FCSTD DOCUMENT  (FreeCAD 1.0R38806 (Git))
Label: UTDFN-4
License: All rights reserved
LicenseURL: http://en.wikipedia.org/wiki/All_rights_reserved
objects: Sketcher::SketchObject×1, PartDesign::Body×1
note: 3 computed .brp shape members not serialized (recipe doc carries the construction recipe); baked Part::Feature solids carry a one-line shape summary decoded from their .brp

FEATURE [Sketcher::SketchObject] Sketch
  ArcFitTolerance = 1e-06
  AttachmentSupport = -> [XY_Plane]
  FullyConstrained = false
  MakeInternals = false
  MapMode = 5
  sketch-geometry (40):
    g0: LineSegment StartX=0 StartY=0.339411 StartZ=0 EndX=-0.339411 EndY=0 EndZ=0
    g1: LineSegment StartX=-0.339411 StartY=0 StartZ=0 EndX=0 EndY=-0.339411 EndZ=0
    g2: LineSegment StartX=0 StartY=-0.339411 StartZ=0 EndX=0.0707107 EndY=-0.268701 EndZ=0
    g3: LineSegment StartX=0.339411 StartY=0 StartZ=0 EndX=0 EndY=0.339411 EndZ=0
    g4: Circle [constr] CenterX=0 CenterY=0 CenterZ=0 NormalX=0 NormalY=0 NormalZ=1 AngleXU=0 Radius=0.339411
    g5: LineSegment [constr] StartX=-0.689647 StartY=-0.350236 StartZ=0 EndX=0.278575 EndY=0.617986 EndZ=0
    g6: LineSegment [constr] StartX=-0.310589 StartY=-0.65 StartZ=0 EndX=0.770537 EndY=0.431126 EndZ=0
    g7: LineSegment [constr] StartX=0.56807 StartY=-0.228658 StartZ=0 EndX=-0.256476 EndY=0.595887 EndZ=0
    g8: LineSegment [constr] StartX=-0.605191 StartY=0.26578 StartZ=0 EndX=0.310589 EndY=-0.65 EndZ=0
    g9: LineSegment [constr] StartX=-0.027746 StartY=-0.65 StartZ=0 EndX=0.673358 EndY=0.0511041 EndZ=0
    g10: LineSegment [constr] StartX=-0.650384 StartY=-0.0281301 StartZ=0 EndX=0.027746 EndY=0.65 EndZ=0
    g11: LineSegment [constr] StartX=-0.027746 StartY=0.65 StartZ=0 EndX=0.785591 EndY=-0.163337 EndZ=0
    g12: LineSegment [constr] StartX=-0.772254 StartY=0.15 StartZ=0 EndX=0.027746 EndY=-0.65 EndZ=0
    g13: LineSegment [constr] StartX=-0.325 StartY=0.65 StartZ=0 EndX=-0.325 EndY=-0.65 EndZ=0
    g14: LineSegment [constr] StartX=-0.325 StartY=-0.65 StartZ=0 EndX=0.325 EndY=-0.65 EndZ=0
    g15: LineSegment [constr] StartX=0.325 StartY=-0.65 StartZ=0 EndX=0.325 EndY=0.65 EndZ=0
    g16: LineSegment [constr] StartX=0.325 StartY=0.65 StartZ=0 EndX=-0.325 EndY=0.65 EndZ=0
    g17: LineSegment StartX=0.2 StartY=-0.65 StartZ=0 EndX=0.45 EndY=-0.65 EndZ=0
    g18: LineSegment StartX=0.45 StartY=-0.65 StartZ=0 EndX=0.45 EndY=-0.25 EndZ=0
    g19: LineSegment StartX=0.45 StartY=-0.25 StartZ=0 EndX=0.372254 EndY=-0.25 EndZ=0
    g20: LineSegment StartX=-0.2 StartY=-0.65 StartZ=0 EndX=-0.2 EndY=-0.422254 EndZ=0
    g21: LineSegment StartX=-0.45 StartY=-0.25 StartZ=0 EndX=-0.45 EndY=-0.65 EndZ=0
    g22: LineSegment StartX=-0.45 StartY=-0.65 StartZ=0 EndX=-0.2 EndY=-0.65 EndZ=0
    g23: LineSegment StartX=-0.2 StartY=0.65 StartZ=0 EndX=-0.45 EndY=0.65 EndZ=0
    g24: LineSegment StartX=-0.45 StartY=0.65 StartZ=0 EndX=-0.45 EndY=0.25 EndZ=0
    g25: LineSegment StartX=-0.45 StartY=0.25 StartZ=0 EndX=-0.372254 EndY=0.25 EndZ=0
    g26: LineSegment StartX=0.2 StartY=0.65 StartZ=0 EndX=0.2 EndY=0.422254 EndZ=0
    g27: LineSegment StartX=0.372254 StartY=0.25 StartZ=0 EndX=0.45 EndY=0.25 EndZ=0
    g28: LineSegment StartX=0.45 StartY=0.25 StartZ=0 EndX=0.45 EndY=0.65 EndZ=0
    g29: LineSegment StartX=0.45 StartY=0.65 StartZ=0 EndX=0.2 EndY=0.65 EndZ=0
    g30: LineSegment StartX=-0.372254 StartY=-0.25 StartZ=0 EndX=-0.2 EndY=-0.422254 EndZ=0
    g31: LineSegment StartX=0.2 StartY=-0.422254 StartZ=0 EndX=0.372254 EndY=-0.25 EndZ=0
    g32: LineSegment StartX=-0.372254 StartY=0.25 StartZ=0 EndX=-0.2 EndY=0.422254 EndZ=0
    g33: LineSegment StartX=0.2 StartY=0.422254 StartZ=0 EndX=0.372254 EndY=0.25 EndZ=0
    g34: LineSegment StartX=-0.2 StartY=0.539411 StartZ=0 EndX=-0.2 EndY=0.65 EndZ=0
    g35: LineSegment StartX=0.2 StartY=-0.422254 StartZ=0 EndX=0.2 EndY=-0.65 EndZ=0
    g36: LineSegment StartX=-0.372254 StartY=-0.25 StartZ=0 EndX=-0.45 EndY=-0.25 EndZ=0
    g37: LineSegment StartX=-0.2 StartY=0.539411 StartZ=0 EndX=-0.2 EndY=0.422254 EndZ=0
    g38: ArcOfCircle CenterX=0.106066 CenterY=-0.233345 CenterZ=0 NormalX=0 NormalY=0 NormalZ=1 AngleXU=0 Radius=0.05 StartAngle=0.785398 EndAngle=3.92699
    g39: LineSegment StartX=0.141421 StartY=-0.19799 StartZ=0 EndX=0.339411 EndY=0 EndZ=0
  constraints (120):
    c: Coincident(g0,g1)
    c: Coincident(g1,g2)
    c: Coincident(g39,g3)
    c: Coincident(g3,g0)
    c: Equal(g0,g1)
    c: Equal(g0,g3)
    c: PointOnObject(g0,g4)
    c: PointOnObject(g1,g4)
    c: PointOnObject(g39,g4)
    c: PointOnObject(g3,g4)
    c: Coincident(g4,g-1)
    c: PointOnObject(g3,g-2)
    c: Distance(g3,g3) = 0.48
    c: Parallel(g8,g7)
    c: Parallel(g6,g5)
    c: PointOnObject(g0,g5)
    c: PointOnObject(g39,g6)
    c: PointOnObject(g1,g6)
    c: Perpendicular(g5,g8)
    c: PointOnObject(g1,g8)
    c: PointOnObject(g0,g7)
    c: Parallel(g12,g8)
    c: Parallel(g7,g11)
    c: Parallel(g10,g5)
    c: Parallel(g9,g6)
    c: Distance(g6,g9) = 0.2
    c: Distance(g11,g7) = 0.2
    c: Distance(g5,g10) = 0.2
    c: Distance(g8,g12) = 0.2
    c: Coincident(g13,g14)
    c: Coincident(g14,g15)
    c: Coincident(g15,g16)
    c: Coincident(g16,g13)
    c: Vertical(g13)
    c: Horizontal(g16)
    c: DistanceY(g15,g15) = 1.3
    c: Symmetric(g14,g15,g-1)
    c: PointOnObject(g10,g16)
    c: PointOnObject(g11,g16)
    c: DistanceX(g14,g14) = 0.65
    c: Symmetric(g14,g13,g-2)
    c: PointOnObject(g9,g14)
    c: PointOnObject(g12,g14)
    c: PointOnObject(g8,g14)
    c: PointOnObject(g6,g14)
    c: Coincident(g17,g18)
    c: Coincident(g18,g19)
    c: Coincident(g35,g17)
    c: Vertical(g18)
    c: Distance(g18,g35) = 0.25
    c: PointOnObject(g17,g14)
    c: Coincident(g36,g21)
    c: Coincident(g21,g22)
    c: Coincident(g22,g20)
    c: Vertical(g20)
    c: Vertical(g21)
    c: Distance(g20,g21) = 0.25
    c: Coincident(g23,g24)
    c: Coincident(g24,g25)
    c: Coincident(g34,g23)
    c: Vertical(g24)
    c: Distance(g24,g34) = 0.25
    c: PointOnObject(g23,g16)
    c: Coincident(g27,g28)
    c: Coincident(g28,g29)
    c: Coincident(g29,g26)
    c: Vertical(g26)
    c: Vertical(g28)
    c: Distance(g26,g28) = 0.25
    c: PointOnObject(g26,g16)
    c: Equal(g21,g24)
    c: Equal(g24,g28)
    c: Equal(g28,g18)
    c: DistanceY(g18,g18) = 0.4
    c: PointOnObject(g20,g14)
    c: Symmetric(g12,g12,g30)
    c: PointOnObject(g30,g12)
    c: PointOnObject(g31,g9)
    c: PointOnObject(g31,g9)
    c: PointOnObject(g32,g10)
    c: PointOnObject(g32,g10)
    c: PointOnObject(g33,g11)
    c: PointOnObject(g33,g11)
    c: PointOnObject(g33,g27)
    c: PointOnObject(g32,g34)
    c: PointOnObject(g32,g25)
    c: PointOnObject(g30,g36)
    c: PointOnObject(g30,g20)
    c: PointOnObject(g31,g35)
    c: PointOnObject(g31,g19)
    c: PointOnObject(g25,g10)
    c: PointOnObject(g34,g7)
    c: Coincident(g26,g33)
    c: PointOnObject(g27,g11)
    c: PointOnObject(g35,g9)
    c: PointOnObject(g19,g9)
    c: PointOnObject(g20,g12)
    c: PointOnObject(g36,g12)
    c: Coincident(g37,g32)
    c: Vertical(g37)
    c: Coincident(g37,g34)
    c: Symmetric(g23,g23,g13)
    c: Horizontal(g25)
    c: Symmetric(g26,g28,g15)
    c: Horizontal(g27)
    c: Symmetric(g20,g21,g13)
    c: Horizontal(g36)
    c: Symmetric(g17,g17,g15)
    c: Vertical(g35)
    c: Horizontal(g19)
    c: PointOnObject(g38,g2)
    c: Diameter(g38) = 0.1
    c: PointOnObject(g38,g6)
    c: PointOnObject(g38,g39)
    c: PointOnObject(g2,g38)
    c: PointOnObject(g39,g38)
    c: Parallel(g1,g8)
    c: Parallel(g6,g39)
    c: Parallel(g2,g6)
    c: Distance(g2,g2) = 0.1
FEATURE [PartDesign::Body] Body
  AllowCompound = false
  Group = -> [Sketch]
  Origin = -> Origin
